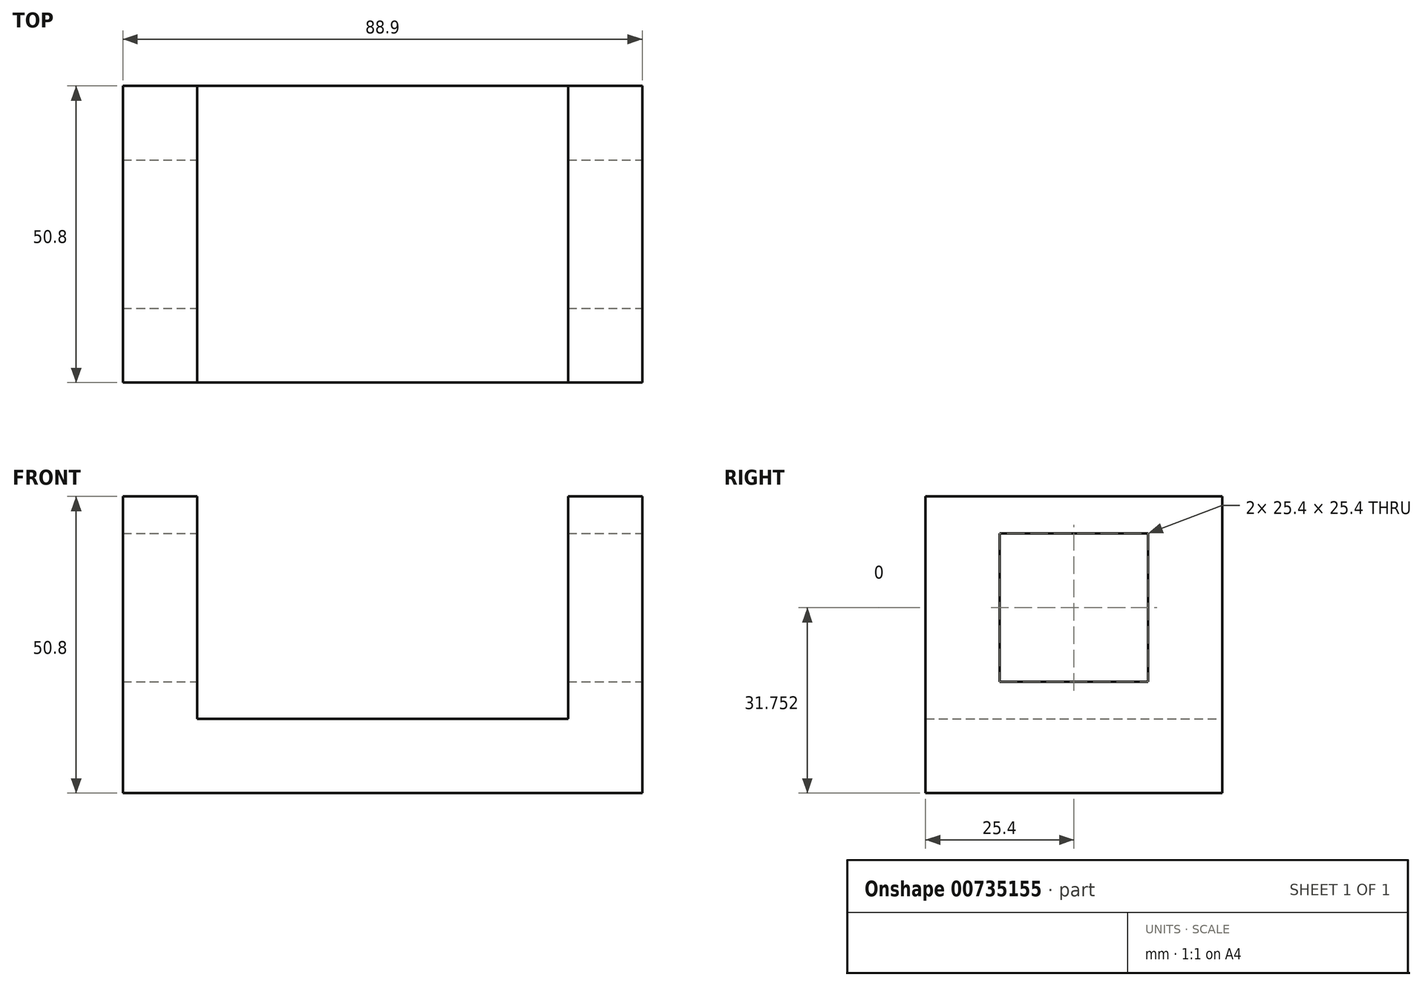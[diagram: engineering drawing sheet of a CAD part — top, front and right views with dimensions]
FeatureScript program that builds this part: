
annotation { "Feature Type Name" : "Feature", "Feature Type Description" : "" }
export const myFeature = defineFeature(function(context is Context, id is Id, definition is map)
    precondition{}
    {
        {
            var Q0;
            Q0=qCreatedBy(makeId("Front.planeOp"),FACE);
            var sketch = newSketch(context, id + "F0", { "sketchPlane" : qUnion([Q0])});
            skLineSegment(sketch, "E0", {"start": v(-70.13, 35.7) * mm, "end": v(-57.43, 35.7) * mm});
            skLineSegment(sketch, "E1", {"start": v(-57.43, 35.7) * mm, "end": v(-57.43, -2.4) * mm});
            skLineSegment(sketch, "E2", {"start": v(-57.43, -2.4) * mm, "end": v(6.07, -2.4) * mm});
            skLineSegment(sketch, "E3", {"start": v(6.07, -2.4) * mm, "end": v(6.07, 35.7) * mm});
            skLineSegment(sketch, "E4", {"start": v(6.07, 35.7) * mm, "end": v(18.77, 35.7) * mm});
            skLineSegment(sketch, "E5", {"start": v(18.77, 35.7) * mm, "end": v(18.77, -15.1) * mm});
            skLineSegment(sketch, "E6", {"start": v(18.77, -15.1) * mm, "end": v(-70.13, -15.1) * mm});
            skLineSegment(sketch, "E7", {"start": v(-70.13, -15.1) * mm, "end": v(-70.13, 35.7) * mm});
            skSolve(sketch);
        }
        {
            var Q0;
            Q0=makeQuery(id+"F0.imprint","IMPRINT",FACE,{"disambiguationData":[TD([[makeQuery(id+"F0.imprint","IMPRINT",EDGE,{"derivedFrom":sQuery(id+"F0.wireOp",EDGE,"E0")}),-1.0]])]});
            extrude(context, id + "F1", {"entities" : qUnion([Q0]), "depth" : 50.8 * mm, "offsetDistance" : 25.4 * mm});
        }
        {
            var Q0;
            Q0=makeQuery(id+"F1.opExtrude","SWEPT_FACE",FACE,{"disambiguationData":[OSD([sQuery(id+"F0.wireOp",EDGE,"E5")])]});
            var sketch = newSketch(context, id + "F2", { "sketchPlane" : qUnion([Q0])});
            skLineSegment(sketch, "E8.bottom", {"start": v(-38.1, 29.35) * mm, "end": v(-12.7, 29.35) * mm});
            skLineSegment(sketch, "E8.top", {"start": v(-38.1, 3.95) * mm, "end": v(-12.7, 3.95) * mm});
            skLineSegment(sketch, "E8.left", {"start": v(-38.1, 29.35) * mm, "end": v(-38.1, 3.95) * mm});
            skLineSegment(sketch, "E8.right", {"start": v(-12.7, 29.35) * mm, "end": v(-12.7, 3.95) * mm});
            skSolve(sketch);
        }
        {
            var Q0;
            Q0=makeQuery(id+"F2.imprint","IMPRINT",FACE,{"disambiguationData":[TD([[makeQuery(id+"F2.imprint","IMPRINT",EDGE,{"derivedFrom":sQuery(id+"F2.wireOp",EDGE,"E8.bottom")}),-1.0]])]});
            extrude(context, id + "F3", {"entities" : qUnion([Q0]), "operationType" : NewBodyOperationType.REMOVE, "oppositeDirection" : true, "depth" : 88.9 * mm, "offsetDistance" : 25.4 * mm});
        }
    });
